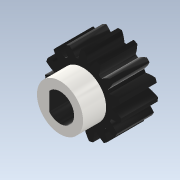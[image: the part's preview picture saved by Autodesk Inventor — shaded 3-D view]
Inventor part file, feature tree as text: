
AUTODESK INVENTOR PART (.ipt)
format: ipt  version: 2020.2 (Build 242310000, 310)  size: 221,184 bytes
history: native  units: mm (DEFAULTED — no unit token found)
features: extrude x3, plane x3, other x3, sketch x3
ambient origin geometry x8: Origin, YZ Plane, XZ Plane, XY Plane, X Axis, Y Axis, Z Axis, Center Point
bodies: Solid1 (feature_tree)
feature tree (12):
  extrude  "Extrusion1"  Depth=8.0mm TaperAngle=0.0deg
  plane  "Work Plane2"
  plane  "Work Plane8"
  plane  "Work Plane9"
  other  "Spur Gear"
  extrude  "Extrusion2"  Depth=10.0mm TaperAngle=0.0deg
  extrude  "Extrusion3"  Depth=5.0mm TaperAngle=0.0deg
  sketch  "Sketch1"  dims[d0=16.5mm d1=8.0mm d2=0.0mm]
  sketch  "Sketch2"  dims[d3=15.0mm d4=10.0mm d5=0.0mm]
  other  "Srf1"
  sketch  "Sketch4"  dims[d16=15.0mm d17=0.0mm d34=2.094395mm d39=0.0mm d41=0.0mm d43=15.0mm d46=15.0mm d47=0.0mm d48=0.0mm d49=6.1mm d53=0.0mm d54=0.0mm d55=5.4mm d56=10.0mm d57=5.0mm d58=0.0mm]
  other  "Pitch Diameter"
